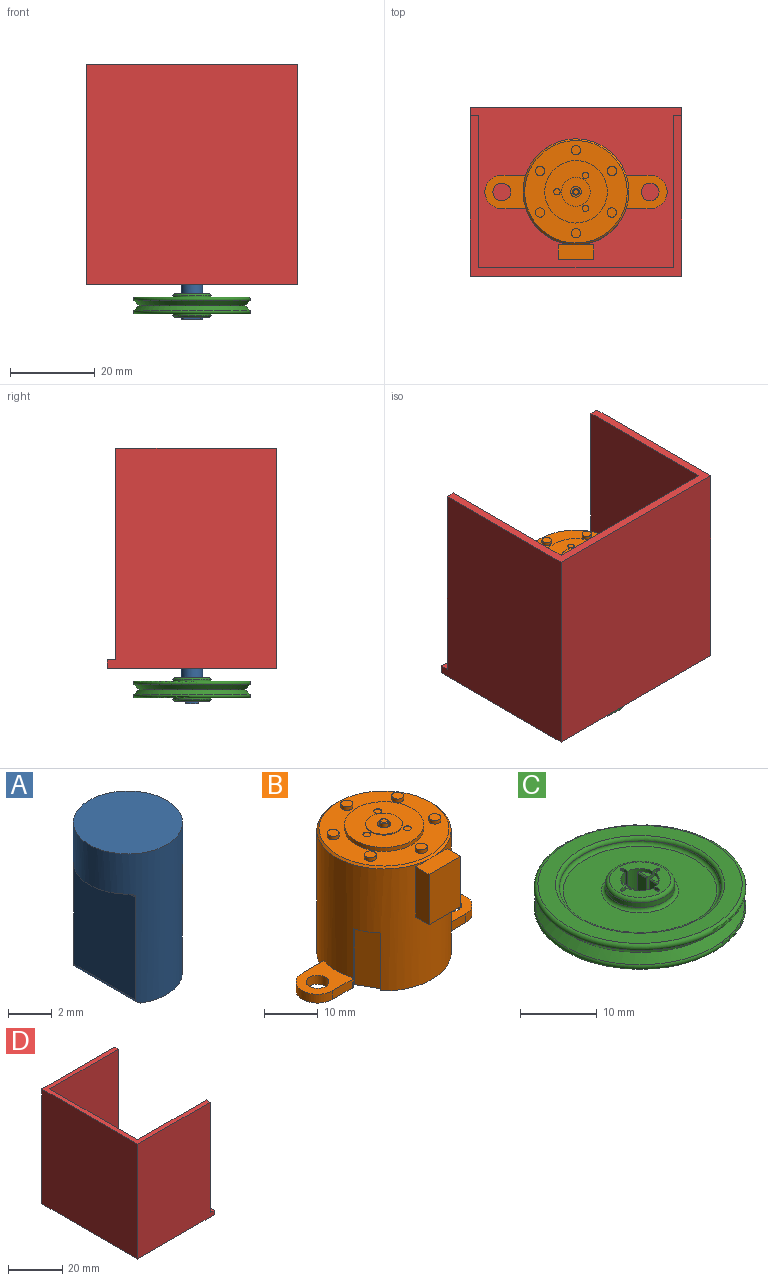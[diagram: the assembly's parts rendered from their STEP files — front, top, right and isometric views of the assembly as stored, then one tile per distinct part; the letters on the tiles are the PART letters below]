
ASSEMBLY  parts=4 mates=3
PART A: 11 faces, bbox 5x5x8.4 mm
  f0: cylinder r=2.5mm len=8.4mm, axis (0,0,1), area 74.9mm2, adj f1,f2,f3,f4,f5,f6,f7,f8
  f1: plane 5x2.6mm, normal (0,0,-1), area 12.4mm2, adj f0,f9,f10
  f2: plane 5x5mm, normal (0,0,1), area 19.6mm2, adj f0
  f3: plane 3.67x0.8mm, normal (0,0,-1), area 2mm2, adj f0,f7
  f4: plane 5.75x4mm, normal (1,0,0), area 23mm2, adj f0,f7,f9
  f5: plane 3.67x0.8mm, normal (0,0,-1), area 2mm2, adj f0,f8
  f6: plane 5.75x4mm, normal (-1,0,0), area 23mm2, adj f0,f8,f10
  f7: cylinder r=0.2mm len=4mm, axis (0,1,0), area 1.2mm2, adj f0,f3,f4
  f8: cylinder r=0.2mm len=4mm, axis (0,-1,0), area 1.2mm2, adj f0,f5,f6
  f9: cylinder r=0.2mm len=4.27mm, axis (0,-1,0), area 1.3mm2, adj f0,f1,f4
  f10: cylinder r=0.2mm len=4.27mm, axis (0,1,0), area 1.3mm2, adj f0,f1,f6
PART B: 66 faces, bbox 43x28.5x32 mm
  f0: cylinder r=12.5mm len=27.8mm, axis (0,0,-1), area 1919.1mm2, adj f1,f3,f4,f5,f8,f11,f13,f16
  f1: plane 43x24.72mm, normal (0,0,-1), area 504mm2, adj f0,f4,f5,f6,f7,f8,f9,f10
  f2: plane 24.2x24.2mm, normal (0,0,1), area 266.3mm2, adj f29,f39,f41,f43,f45,f47,f49,f51
  f3: plane 5.25x1mm, normal (0,0,-1), area 4.8mm2, adj f0,f4,f5,f6
  f4: plane 13.2x0.72mm, normal (-1,0,0), area 9.5mm2, adj f0,f1,f3,f6
  f5: plane 13.2x0.72mm, normal (1,0,0), area 9.5mm2, adj f0,f1,f3,f6
  f6: plane 13.2x5.25mm, normal (0,1,0), area 69.3mm2, adj f1,f3,f4,f5
  f7: plane 5.38x2mm, normal (0,-1,0), area 10.8mm2, adj f1,f10,f11,f25
  f8: plane 5.66x2mm, normal (0,1,0), area 11.3mm2, adj f0,f1,f10,f11
  f9: cylinder r=2.1mm len=4.2mm, axis (0,0,-1), area 26.4mm2, adj f1,f11
  f10: cylinder r=4mm len=8mm, axis (0,0,-1), area 25.1mm2, adj f1,f7,f8,f11
  f11: plane 9.66x8mm, normal (0,0,1), area 53mm2, adj f0,f7,f8,f9,f10,f24,f25
  f12: cylinder r=4mm len=8mm, axis (0,0,-1), area 25.1mm2, adj f1,f13,f14,f16
  f13: plane 5.66x2mm, normal (0,1,0), area 11.3mm2, adj f0,f1,f12,f16
  f14: plane 5.38x2mm, normal (0,-1,0), area 10.8mm2, adj f1,f12,f16,f19
  f15: cylinder r=2.1mm len=4.2mm, axis (0,0,-1), area 26.4mm2, adj f1,f16
  f16: plane 9.66x8mm, normal (0,0,1), area 53mm2, adj f0,f12,f13,f14,f15,f19,f20
  f17: plane 4.91x3.25mm, normal (0,0,-1), area 4.8mm2, adj f0,f18,f20,f21
  f18: plane 13.2x0.62mm, normal (0.5,0.87,0), area 9.5mm2, adj f0,f1,f17,f21
  f19: plane 2x0.02mm, normal (-0.87,0.5,0), area 0.1mm2, adj f1,f14,f16,f20
  f20: plane 13.2x0.87mm, normal (-0.5,-0.87,0), area 10.1mm2, adj f0,f1,f16,f17,f19,f21
  f21: plane 13.2x4.55mm, normal (0.87,-0.5,0), area 69.3mm2, adj f1,f17,f18,f20
  f22: plane 4.91x3.25mm, normal (0,0,-1), area 4.8mm2, adj f0,f23,f24,f26
  f23: plane 13.2x0.62mm, normal (-0.5,0.87,0), area 9.5mm2, adj f0,f1,f22,f26
  f24: plane 13.2x0.87mm, normal (0.5,-0.87,0), area 10.1mm2, adj f0,f1,f11,f22,f25,f26
  f25: plane 2x0.02mm, normal (0.87,0.5,0), area 0.1mm2, adj f1,f7,f11,f24
  f26: plane 13.2x4.55mm, normal (-0.87,-0.5,0), area 69.3mm2, adj f1,f22,f23,f24
  f27: cylinder r=5mm len=10mm, axis (0,0,1), area 62.8mm2, adj f1,f28
  f28: plane 10x10mm, normal (0,0,-1), area 78.5mm2, adj f27
  f29: cone r=12.1mm half-angle=45deg, axis (0,0,-1), area 43.7mm2, adj f0,f2,f38
  f30: plane 11.45x0.04mm, normal (1,0,0), area 0.5mm2, adj f0,f32,f37,f38
  f31: plane 11.45x0.04mm, normal (-1,0,0), area 0.5mm2, adj f0,f33,f37,f38
  f32: plane 11.45x3.15mm, normal (0,1,0), area 36.1mm2, adj f30,f36,f37,f38
  f33: plane 11.45x3.15mm, normal (0,1,0), area 36.1mm2, adj f31,f34,f37,f38
  f34: plane 11.45x3.5mm, normal (-1,0,0), area 40.1mm2, adj f33,f35,f37,f38
  f35: plane 11.45x8.3mm, normal (0,-1,0), area 95mm2, adj f34,f36,f37,f38
  f36: plane 11.45x3.5mm, normal (1,0,0), area 40.1mm2, adj f32,f35,f37,f38
  f37: plane 8.3x3.54mm, normal (0,0,-1), area 29.1mm2, adj f0,f30,f31,f32,f33,f34,f35,f36
  f38: plane 8.3x3.54mm, normal (0,0,1), area 29.1mm2, adj f29,f30,f31,f32,f33,f34,f35,f36
  f39: cylinder r=1.1mm len=2.2mm, axis (0,0,-1), area 5.5mm2, adj f2,f40
  f40: plane 2.2x2.2mm, normal (0,0,1), area 3.8mm2, adj f39
  f41: cylinder r=1.1mm len=2.2mm, axis (0,0,-1), area 5.5mm2, adj f2,f42
  f42: plane 2.2x2.2mm, normal (0,0,1), area 3.8mm2, adj f41
  f43: cylinder r=1.1mm len=2.2mm, axis (0,0,-1), area 5.5mm2, adj f2,f44
  f44: plane 2.2x2.2mm, normal (0,0,1), area 3.8mm2, adj f43
  f45: cylinder r=1.1mm len=2.2mm, axis (0,0,-1), area 5.5mm2, adj f2,f46
  f46: plane 2.2x2.2mm, normal (0,0,1), area 3.8mm2, adj f45
  f47: cylinder r=1.1mm len=2.2mm, axis (0,0,-1), area 5.5mm2, adj f2,f48
  f48: plane 2.2x2.2mm, normal (0,0,1), area 3.8mm2, adj f47
  f49: cylinder r=1.1mm len=2.2mm, axis (0,0,-1), area 5.5mm2, adj f2,f50
  f50: plane 2.2x2.2mm, normal (0,0,1), area 3.8mm2, adj f49
  f51: cylinder r=7.38mm len=14.75mm, axis (0,0,-1), area 41.7mm2, adj f2,f52
  f52: plane 14.75x14.75mm, normal (0,0,1), area 129.3mm2, adj f51,f53,f60,f62,f64
  f53: cylinder r=3.4mm len=6.8mm, axis (0,0,-1), area 4.3mm2, adj f52,f54
  f54: plane 6.8x6.8mm, normal (0,0,1), area 31.4mm2, adj f53,f56
  f55: plane 2.5x2.5mm, normal (0,0,1), area 2.9mm2, adj f56,f57
  f56: cylinder r=1.25mm len=2.5mm, axis (0,0,1), area 8.6mm2, adj f54,f55
  f57: cylinder r=0.8mm len=1.6mm, axis (0,0,-1), area 8mm2, adj f55,f59
  f58: plane 1.2x1.2mm, normal (0,0,1), area 1.1mm2, adj f59
  f59: torus R=0.6mm, axis (0,0,1), area 1.4mm2, adj f57,f58
  f60: cylinder r=0.75mm len=1.5mm, axis (0,0,1), area 0.5mm2, adj f52,f61
  f61: plane 1.5x1.5mm, normal (0,0,1), area 1.8mm2, adj f60
  f62: cylinder r=0.75mm len=1.5mm, axis (0,0,1), area 0.5mm2, adj f52,f63
  f63: plane 1.5x1.5mm, normal (0,0,1), area 1.8mm2, adj f62
  f64: cylinder r=0.75mm len=1.5mm, axis (0,0,1), area 0.5mm2, adj f52,f65
  f65: plane 1.5x1.5mm, normal (0,0,1), area 1.8mm2, adj f64
PART C: 64 faces, bbox 29.9x29.9x5.5 mm
  f0: plane 8x8mm, normal (0,0,-1), area 28.7mm2, adj f2,f8,f9,f15,f35,f44,f45,f46
  f1: plane 8x8mm, normal (0,0,1), area 28.7mm2, adj f2,f8,f9,f15,f34,f44,f45,f46
  f2: cylinder r=2.5mm len=5.5mm, axis (0,0,1), area 9.6mm2, adj f0,f1,f3,f4,f5,f6,f7,f58
  f3: plane 4.1x1.75mm, normal (-1,0,0), area 7.2mm2, adj f2,f6,f7,f62
  f4: plane 1.58x0.79mm, normal (0,0,1), area 0.8mm2, adj f2,f7,f62
  f5: plane 1.58x0.79mm, normal (0,0,-1), area 0.8mm2, adj f2,f6,f62
  f6: cylinder r=0.2mm len=1.75mm, axis (0,-1,0), area 0.5mm2, adj f2,f3,f5,f62
  f7: cylinder r=0.2mm len=1.75mm, axis (0,-1,0), area 0.5mm2, adj f2,f3,f4,f62
  f8: cylinder r=2.5mm len=5.5mm, axis (0,0,1), area 9.6mm2, adj f0,f1,f17,f26,f28,f40,f42,f53
  f9: cylinder r=2.5mm len=5.5mm, axis (0,0,1), area 9.6mm2, adj f0,f1,f10,f11,f12,f13,f14,f48
  f10: plane 4.1x1.75mm, normal (1,0,0), area 7.2mm2, adj f9,f13,f14,f52
  f11: plane 1.58x0.79mm, normal (0,0,1), area 0.8mm2, adj f9,f14,f52
  f12: plane 1.58x0.79mm, normal (0,0,-1), area 0.8mm2, adj f9,f13,f52
  f13: cylinder r=0.2mm len=1.75mm, axis (0,1,0), area 0.5mm2, adj f9,f10,f12,f52
  f14: cylinder r=0.2mm len=1.75mm, axis (0,1,0), area 0.5mm2, adj f9,f10,f11,f52
  f15: cylinder r=2.5mm len=5.5mm, axis (0,0,1), area 9.6mm2, adj f0,f1,f16,f27,f29,f41,f43,f47
  f16: plane 4.1x1.75mm, normal (-1,0,0), area 7.2mm2, adj f15,f41,f43,f63
  f17: plane 4.1x1.75mm, normal (1,0,0), area 7.2mm2, adj f8,f40,f42,f53
  f18: cone r=12.5mm half-angle=45deg, axis (0,0,-1), area 133.2mm2, adj f19,f39
  f19: cone r=12.5mm half-angle=45deg, axis (0,0,1), area 133.2mm2, adj f18,f30
  f20: plane 26.59x26.59mm, normal (0,0,1), area 175mm2, adj f30,f32
  f21: plane 20x20mm, normal (0,0,1), area 235.6mm2, adj f31,f33
  f22: cylinder r=4.5mm len=9mm, axis (0,0,-1), area 21.2mm2, adj f33,f34
  f23: cylinder r=4.5mm len=9mm, axis (0,0,-1), area 21.2mm2, adj f35,f36
  f24: plane 20x20mm, normal (0,0,-1), area 235.6mm2, adj f36,f38
  f25: plane 26.59x26.59mm, normal (0,0,-1), area 175mm2, adj f37,f39
  f26: plane 1.58x0.79mm, normal (0,0,1), area 0.8mm2, adj f8,f42,f53
  f27: plane 1.58x0.79mm, normal (0,0,1), area 0.8mm2, adj f15,f43,f63
  f28: plane 1.58x0.79mm, normal (0,0,-1), area 0.8mm2, adj f8,f40,f53
  f29: plane 1.58x0.79mm, normal (0,0,-1), area 0.8mm2, adj f15,f41,f63
  f30: torus R=13.29mm, axis (0,0,1), area 101.1mm2, adj f19,f20
  f31: torus R=10mm, axis (0,0,1), area 50.9mm2, adj f21,f32
  f32: torus R=11mm, axis (0,0,1), area 52.7mm2, adj f20,f31
  f33: torus R=5mm, axis (0,0,1), area 23.1mm2, adj f21,f22
  f34: torus R=4mm, axis (0,0,1), area 21.3mm2, adj f1,f22
  f35: torus R=4mm, axis (0,0,1), area 21.3mm2, adj f0,f23
  f36: torus R=5mm, axis (0,0,1), area 23.1mm2, adj f23,f24
  f37: torus R=11mm, axis (0,0,1), area 52.7mm2, adj f25,f38
  f38: torus R=10mm, axis (0,0,1), area 50.9mm2, adj f24,f37
  f39: torus R=13.29mm, axis (0,0,1), area 101.1mm2, adj f18,f25
  f40: cylinder r=0.2mm len=1.75mm, axis (0,1,0), area 0.5mm2, adj f8,f17,f28,f53
  f41: cylinder r=0.2mm len=1.75mm, axis (0,-1,0), area 0.5mm2, adj f15,f16,f29,f63
  f42: cylinder r=0.2mm len=1.75mm, axis (0,1,0), area 0.5mm2, adj f8,f17,f26,f53
  f43: cylinder r=0.2mm len=1.75mm, axis (0,-1,0), area 0.5mm2, adj f15,f16,f27,f63
  f44: cylinder r=0.2mm len=5.5mm, axis (0,0,1), area 1.7mm2, adj f0,f1,f45,f47
  f45: plane 5.5x0.1mm, normal (0,-1,0), area 0.6mm2, adj f0,f1,f44,f46
  f46: cylinder r=0.2mm len=5.5mm, axis (0,0,1), area 1.7mm2, adj f0,f1,f45,f48
  f47: plane 5.5x0.8mm, normal (-1,0,0), area 4.4mm2, adj f0,f1,f15,f44
  f48: plane 5.5x0.8mm, normal (1,0,0), area 4.4mm2, adj f0,f1,f9,f46
  f49: cylinder r=0.2mm len=5.5mm, axis (0,0,1), area 1.7mm2, adj f0,f1,f50,f52
  f50: plane 5.5x0.1mm, normal (1,0,0), area 0.6mm2, adj f0,f1,f49,f51
  f51: cylinder r=0.2mm len=5.5mm, axis (0,0,1), area 1.7mm2, adj f0,f1,f50,f53
  f52: plane 5.5x1.79mm, normal (0,-1,0), area 8.8mm2, adj f0,f1,f9,f10,f11,f12,f13,f14
  f53: plane 5.5x1.79mm, normal (0,1,0), area 8.8mm2, adj f0,f1,f8,f17,f26,f28,f40,f42
  f54: cylinder r=0.2mm len=5.5mm, axis (0,0,1), area 1.7mm2, adj f0,f1,f55,f57
  f55: plane 5.5x0.1mm, normal (0,1,0), area 0.6mm2, adj f0,f1,f54,f56
  f56: cylinder r=0.2mm len=5.5mm, axis (0,0,1), area 1.7mm2, adj f0,f1,f55,f58
  f57: plane 5.5x0.8mm, normal (1,0,0), area 4.4mm2, adj f0,f1,f8,f54
  f58: plane 5.5x0.8mm, normal (-1,0,0), area 4.4mm2, adj f0,f1,f2,f56
  f59: cylinder r=0.2mm len=5.5mm, axis (0,0,1), area 1.7mm2, adj f0,f1,f60,f62
  f60: plane 5.5x0.1mm, normal (-1,0,0), area 0.6mm2, adj f0,f1,f59,f61
  f61: cylinder r=0.2mm len=5.5mm, axis (0,0,1), area 1.7mm2, adj f0,f1,f60,f63
  f62: plane 5.5x1.79mm, normal (0,1,0), area 8.8mm2, adj f0,f1,f2,f3,f4,f5,f6,f7
  f63: plane 5.5x1.79mm, normal (0,-1,0), area 8.8mm2, adj f0,f1,f15,f16,f27,f29,f41,f43
PART D: 13 faces, bbox 40x50x52 mm
  f0: plane 50x2mm, normal (1,0,0), area 100mm2, adj f1,f3,f5,f6
  f1: plane 52x40mm, normal (0,1,0), area 1980mm2, adj f0,f2,f5,f6,f8,f12
  f2: plane 52x50mm, normal (-1,0,0), area 2600mm2, adj f1,f3,f6,f12
  f3: plane 52x40mm, normal (0,-1,0), area 1980mm2, adj f0,f2,f5,f6,f9,f12
  f4: cylinder r=5mm len=10mm, axis (0,0,-1), area 62.8mm2, adj f5,f6
  f5: plane 50x38mm, normal (0,0,1), area 1677.5mm2, adj f0,f1,f3,f4,f7,f8,f9,f10
  f6: plane 50x40mm, normal (0,0,-1), area 1921.5mm2, adj f0,f1,f2,f3,f4
  f7: plane 50x36mm, normal (0,-1,0), area 1800mm2, adj f5,f8,f11,f12
  f8: plane 50x2mm, normal (1,0,0), area 100mm2, adj f1,f5,f7,f12
  f9: plane 50x2mm, normal (1,0,0), area 100mm2, adj f3,f5,f10,f12
  f10: plane 50x36mm, normal (0,1,0), area 1800mm2, adj f5,f9,f11,f12
  f11: plane 50x46mm, normal (1,0,0), area 2300mm2, adj f5,f7,f10,f12
  f12: plane 50x38mm, normal (0,0,1), area 244mm2, adj f1,f2,f3,f7,f8,f9,f10,f11
PLACE A rot(axis=(0,0,1),88.2deg) t=(4.66,-10.6,-4.45)mm
PLACE B t=(4.66,-10.6,-4.45)mm fixed
PLACE C rot(axis=(0,0,1),88.2deg) t=(4.66,-10.6,-11.45)mm
PLACE D rot(axis=(0,0,1),90deg) t=(4.66,-10.6,-6.45)mm
MATE fastened B.f27 <-> D.f4  axis (0,0,-1) through (4.66,-10.6,-6.45)mm
MATE revolute A.f0 <-> B.f27  axis (0,0,1) through (4.66,-10.6,-6.45)mm
MATE fastened C.f2 <-> A.f0  axis (0,0,1) through (4.66,-10.6,-8.7)mm
